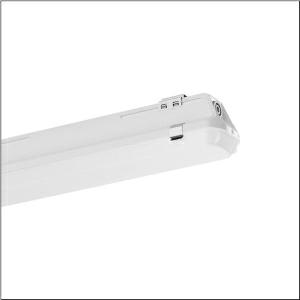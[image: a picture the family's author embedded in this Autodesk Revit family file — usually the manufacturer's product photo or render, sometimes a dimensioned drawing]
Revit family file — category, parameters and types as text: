
# Revit family: monsun_r__21_51fb20ml460j_6258
name_source: partatom
category: Lighting Fixtures
units: mm (PartAtom-declared; Revit-internal decimal feet)

## family parameters
Cut with Voids When Loaded = No
Host = Face
Light Source = No
Part Type = Normal
Room Calculation Point = No
Round Connector Dimension = Use Diameter
Shared = No

## types (1)
- --- (1 x LED, 3840 lm, 25.7 W, 4000K)
    Apparent Load = 26 VA
    CIE Flux Codes = 45 75 93 94 100
    Color Rendering = 80
    Color Temperature = 4000K
    Default Elevation = 1800 mm
    Description = Monsun® 21, damp-proof luminaire, chain hanger, primary optical cover: enclosure, of PC, light emission: direct distribution, primary light characteristic: symmetric, installation type: suspended mounting, surface-mounted, horizontal mounting, vertical mounting, LED, rated luminous flux: 6.030lm, luminous efficacy: 147lm/W, light colour: 840, colour temperature: 4000K, control gear: ECG, with terminal, 3-pole, max. 2.5mm², mains connection: 220..240V, AC, 50/60Hz, rated input power: 41W, housing, of glass-fibre reinforced plastic, uncoated, bright grey, incl. chain hanger, length: 1.299mm, width: 90mm, height: 88mm, clip for enclosure, of stainless steel (V2A), ceiling mounting element, of stainless steel (V2A), chain hanger, of stainless steel (V2A), protection rating (complete): IP66, insulation class (complete): insulation class I (protective earthing), certification: CE, ENEC, VDE, UKCA, protection symbol: D, impact resistance: IK04, permissible operating ambient temperature: -25..+35°C, standard: EN 50419, EN 60598-2-1, corresponds to IFS (International Featured Standards) requirements for safety and quality in the food industry, for indoor or canopied outdoor use, no direct snow, no direct sun, no direct rain, contact your sales advisor before using the luminaires in applications with unclear chemical exposure, large temperature fluctuations or condensation-forming humidity, LABS conformity tested according to VDMA 24364:2018-05, packaging unit: 1 piece
    Height = 88 mm
    Lamp = 1 x LED
    Lamp Light Flux = 3840 lm
    Lamp Power = 25.7 W
    Lamp count = 1
    Length = 1299 mm
    Luminous efficacy = 149 lm/W
    Manufacturer = Siteco
    ModVariant = No
    Model = 51FB20ML460J
    Mounting Place = Ceiling
    Mounting Type = Surface mounted
    Number of Poles = 1
    OnlyDefault = Yes
    Power Factor = 1
    Product Name = Monsun® 21
    Product group = damp-proof luminaire
    ProductGroupID = 300
    Protection Class = Protection class I
    Protection Degree = IP 66
    RLX_Detail_Level = 1
    RLX_Emergency_Light_Flux = 0 lm
    RLX_Emergency_Type = 0
    RLX_Emergency_Type_DB = No
    RlxData = <blob elided: 91001 chars, md5=e411e0bd>
    Socket = socket
    Standby Power = 0 W
    System Light Flux = 3840 lm
    System Power = 26 W
    Type Comments = factory setting: luminous flux: 64 % | (A | C | E) | 59 mA
    Type Image = l_1006717.jpg
    URL = http://relux.com
    VarID = @adj_077927
    Voltage = 0 V
    Weight = 0.00 kg
    Width = 90 mm

## geometry (parser evidence)
native form markers: Blend x4, Sweep x14
no freeform markers — native parametric forms only
